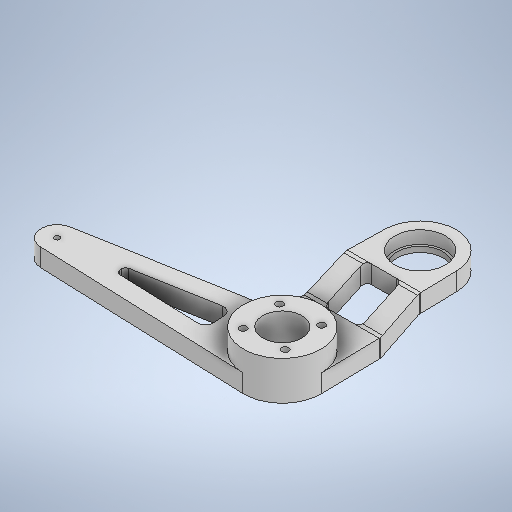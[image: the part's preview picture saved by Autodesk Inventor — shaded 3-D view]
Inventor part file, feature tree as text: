
AUTODESK INVENTOR PART (.ipt)
format: ipt  version: 2025.2 (Build 292293000, 293)  size: 516,096 bytes
history: native  units: mm
features: sketch x12, extrude x11, other x5, fillet x5, projected_geometry x3, loft x2, split x1, move_body x1, boolean_combine x1
ambient origin geometry x8: Origin, YZ Plane, XZ Plane, XY Plane, X Axis, Y Axis, Z Axis, Center Point
bodies: Solid1 (feature_tree), Solid2 (feature_tree), Solid3 (feature_tree)
feature tree (41):
  other  "Brace"
  extrude  "Extrusion1"  Depth=76.5mm
  extrude  "Extrusion2"  Depth=20.0mm
  extrude  "Extrusion3"  Depth=10.0mm TaperAngle=0.0deg
  extrude  "Extrusion4"  Depth=7.0mm TaperAngle=0.0deg
  extrude  "Extrusion5"  TaperAngle=0.0deg  [1 undecoded]
  fillet  "Fillet3"  Radius=117.0mm
  sketch  "Sketch6"  dims[d27=10.0mm d28=0.0mm d31=15.009832mm]
  split  "Split1"
  move_body  "Move Body1"
  extrude  "Extrusion6"  Depth=3.0mm
  sketch  "Sketch8"  dims[d33=10.75mm d34=23.6mm]
  sketch  "Sketch9"  dims[d35=40.0mm d40=0.0mm d41=10.0mm d42=0.0mm]
  extrude  "Extrusion7"  Depth=10.0mm
  extrude  "Extrusion8"  Depth=23.6mm
  loft  "Loft2"
  loft  "Loft3"
  boolean_combine  "Combine2"
  fillet  "Fillet6"  Radius=20.0mm
  fillet  "Fillet7"  Radius=1.0mm
  extrude  "Extrusion9"  TaperAngle=0.0deg  [1 undecoded]
  fillet  "Fillet8"  [1 undecoded]
  fillet  "Fillet9"  Radius=3.0mm
  extrude  "Extrusion10"  Depth=4.5mm
  extrude  "Extrusion11"  TaperAngle=0.0deg  [1 undecoded]
  sketch  "Sketch1"  dims[d0=40.0mm d3=76.5mm]
  sketch  "Sketch2"  dims[d6=10.0mm d7=0.0mm d8=11.5mm d9=0.0mm]
  sketch  "Sketch3"  dims[d10=28.07mm d12=7.0mm d13=0.0mm]
  sketch  "Sketch4"  dims[d14=1.3mm d15=0.0mm d16=0.0mm d17=117.0mm]
  sketch  "Sketch5"  dims[d19=3.0mm d21=18.0mm]
  projected_geometry  "Projected Loop1"
  projected_geometry  "Projected Loop2"
  projected_geometry  "Projected Loop3"
  other  "Edges3"
  other  "Edges4"
  other  "Edges5"
  other  "Edges6"
  sketch  "Sketch10"  dims[d43=0.0mm d44=0.0mm d49=20.0mm d51=20.0mm d53=1.0mm d54=0.0mm]
  sketch  "Sketch11"  dims[d55=1.0mm d56=0.0mm d66=0.0mm d67=90.0deg d68=0.0mm d69=90.0deg]
  sketch  "Sketch12"  dims[d70=0.0mm d71=90.0deg d72=0.0mm d73=90.0deg d75=3.0mm d76=4.5mm d79=0.0mm d80=0.0mm d83=4.5mm d84=2.0mm d85=21.7mm d86=0.0mm d87=0.0mm d88=30.9mm d90=4.0mm d91=40.0mm d93=360.0deg d95=0.0mm d96=0.0mm d97=7.15585mm d36=0.5mm d37=0.872665mm d38=0.5mm d39=0.872665mm d77=0.0mm d78=0.0mm]
  sketch  "Sketch Circular Pattern1"  dims[d4=1.5mm d5=20.0mm]
note: 4 required parameter values undecoded (feature->parameter linkage not recoverable at this tier; creation-order binding heuristic only, values carry confidence <= 0.55)
